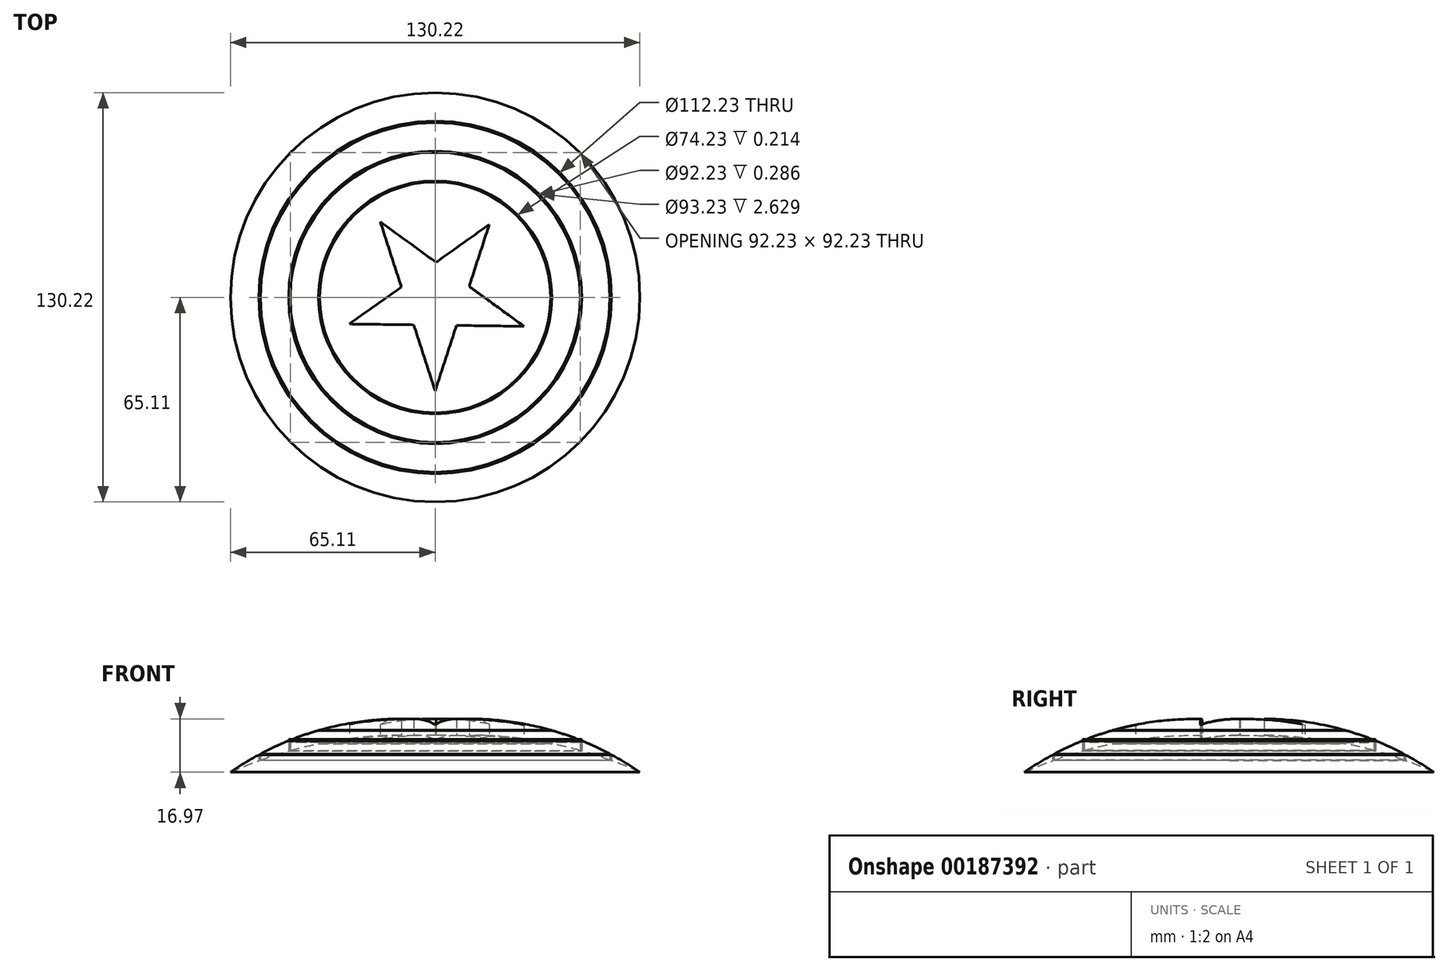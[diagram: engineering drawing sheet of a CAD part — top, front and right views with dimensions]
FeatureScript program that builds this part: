
annotation { "Feature Type Name" : "Feature", "Feature Type Description" : "" }
export const myFeature = defineFeature(function(context is Context, id is Id, definition is map)
    precondition{}
    {
        {
            var Q0;
            Q0=qCreatedBy(makeId("Front.planeOp"),FACE);
            var sketch = newSketch(context, id + "F0", { "sketchPlane" : qUnion([Q0])});
            skArc(sketch, "E0", {"start": v(65.11, 0) * mm, "mid": v(34.05, 14.12) * mm, "end": v(0, 16.34) * mm});
            skLineSegment(sketch, "E1", {"start": v(0, 16.34) * mm, "end": v(0, 11.34) * mm});
            skArc(sketch, "E2", {"start": v(65.11, 0) * mm, "mid": v(33.28, 9.81) * mm, "end": v(0, 11.34) * mm});
            skSolve(sketch);
        }
        {
            var Q0;
            Q0=makeQuery(id+"F0.imprint","IMPRINT",FACE,{"disambiguationData":[TD([[makeQuery(id+"F0.imprint","IMPRINT",EDGE,{"derivedFrom":sQuery(id+"F0.wireOp",EDGE,"E0")}),1.0]])]});
            var Q1;
            Q1=sQuery(id+"F0.wireOp",EDGE,"E1");
            revolve(context, id + "F1", {"entities" : qUnion([Q0]), "axis" : qUnion([Q1]), "revolveType" : RevolveType.FULL});
        }
        {
            var Q0;
            Q0=qCreatedBy(makeId("Top.planeOp"),FACE);
            var sketch = newSketch(context, id + "F2", { "sketchPlane" : qUnion([Q0])});
            skCircle(sketch, "E3", {"center": v(0, 0) * mm, "radius": 56.11 * mm});
            skCircle(sketch, "E4", {"center": v(0, 0) * mm, "radius": 55.61 * mm});
            skCircle(sketch, "E5", {"center": v(0, 0) * mm, "radius": 46.61 * mm});
            skCircle(sketch, "E6", {"center": v(0, 0) * mm, "radius": 46.11 * mm});
            skCircle(sketch, "E7", {"center": v(0, 0) * mm, "radius": 37.11 * mm});
            skCircle(sketch, "E8", {"center": v(0, 0) * mm, "radius": 36.61 * mm});
            skSolve(sketch);
        }
        {
            var Q0;
            Q0=makeQuery(id+"F2.imprint","IMPRINT",FACE,{"disambiguationData":[TD([[makeQuery(id+"F2.imprint","IMPRINT",EDGE,{"derivedFrom":sQuery(id+"F2.wireOp",EDGE,"E3")}),1.0]])]});
            var Q1;
            Q1=makeQuery(id+"F2.imprint","IMPRINT",FACE,{"disambiguationData":[TD([[makeQuery(id+"F2.imprint","IMPRINT",EDGE,{"derivedFrom":sQuery(id+"F2.wireOp",EDGE,"E5")}),1.0]])]});
            var Q2;
            Q2=makeQuery(id+"F2.imprint","IMPRINT",FACE,{"disambiguationData":[TD([[makeQuery(id+"F2.imprint","IMPRINT",EDGE,{"derivedFrom":sQuery(id+"F2.wireOp",EDGE,"E7")}),1.0]])]});
            extrude(context, id + "F3", {"entities" : qUnion([Q0, Q1, Q2]), "operationType" : NewBodyOperationType.REMOVE, "depth" : 9.5 * mm});
        }
        {
            var Q0;
            Q0=qCreatedBy(makeId("Top.planeOp"),FACE);
            var sketch = newSketch(context, id + "F4", { "sketchPlane" : qUnion([Q0])});
            skArc(sketch, "E9.cCircle", {"start": v(-1.88, -24) * mm, "mid": v(0, -24.07) * mm, "end": v(1.86, -24) * mm, "construction": true});
            skLineSegment(sketch, "E9.4", {"start": v(17.5, 24.06) * mm, "end": v(17.66, 23.53) * mm});
            skLineSegment(sketch, "E10", {"start": v(0, -29.75) * mm, "end": v(-6.83, -8.74) * mm});
            skLineSegment(sketch, "E11", {"start": v(0, -29.75) * mm, "end": v(6.77, -8.92) * mm});
            skLineSegment(sketch, "E12", {"start": v(17.66, 23.53) * mm, "end": v(0.28, 11.16) * mm});
            skLineSegment(sketch, "E13", {"start": v(-27.28, -8.47) * mm, "end": v(-6.83, -8.74) * mm});
            skLineSegment(sketch, "E14", {"start": v(28.29, -9.2) * mm, "end": v(10.8, 3.5) * mm});
            skLineSegment(sketch, "E15.trimOffspring", {"start": v(-10.74, 3.31) * mm, "end": v(-28.3, -9.18) * mm});
            skLineSegment(sketch, "E16.trimOffspring", {"start": v(-10.74, 3.31) * mm, "end": v(-17.48, 24.07) * mm});
            skLineSegment(sketch, "E17.trimOffspring", {"start": v(6.77, -8.92) * mm, "end": v(28.29, -9.2) * mm});
            skLineSegment(sketch, "E18.trimOffspring", {"start": v(10.8, 3.5) * mm, "end": v(17.5, 24.06) * mm});
            skLineSegment(sketch, "E19.trimOffspring", {"start": v(0.28, 11.16) * mm, "end": v(-17.48, 24.07) * mm});
            skArc(sketch, "E20.trimOffspring", {"start": v(22.27, -9.12) * mm, "mid": v(22.9, -7.4) * mm, "end": v(23.4, -5.64) * mm, "construction": true});
            skArc(sketch, "E21.trimOffspring", {"start": v(15.62, 18.3) * mm, "mid": v(14.36, 19.31) * mm, "end": v(13.03, 20.23) * mm, "construction": true});
            skArc(sketch, "E22.trimOffspring", {"start": v(-12.58, 20.51) * mm, "mid": v(-14.14, 19.47) * mm, "end": v(-15.6, 18.32) * mm, "construction": true});
            skArc(sketch, "E23.trimOffspring", {"start": v(-23.38, -5.69) * mm, "mid": v(-22.99, -7.12) * mm, "end": v(-22.5, -8.53) * mm, "construction": true});
            skSolve(sketch);
        }
        {
            var Q0;
            Q0=makeQuery(id+"F4.imprint","IMPRINT",FACE,{"disambiguationData":[TD([[makeQuery(id+"F4.imprint","IMPRINT",EDGE,{"derivedFrom":sQuery(id+"F4.wireOp",EDGE,"E10")}),-1.0]])]});
            extrude(context, id + "F5", {"entities" : qUnion([Q0]), "operationType" : NewBodyOperationType.REMOVE, "depth" : 25 * mm});
        }
        {
            var Q0;
            Q0=makeQuery(id+"F3.boolean.opBoolean","COPY",FACE,{"derivedFrom":makeQuery(id+"F3.opExtrude","CAP_FACE",FACE,{"disambiguationData":[OSD([sQuery(id+"F2.wireOp",EDGE,"E7"),sQuery(id+"F2.wireOp",EDGE,"E8")])],"isStart":false})});
            extrude(context, id + "F6", {"entities" : qUnion([Q0]), "operationType" : NewBodyOperationType.ADD, "oppositeDirection" : true, "depth" : 1 * mm, "hasSecondDirection" : true, "secondDirectionOppositeDirection" : false, "secondDirectionDepth" : .1 * mm});
        }
        {
            var Q0;
            Q0=makeQuery(id+"F3.boolean.opBoolean","COPY",FACE,{"derivedFrom":makeQuery(id+"F3.opExtrude","CAP_FACE",FACE,{"disambiguationData":[OSD([sQuery(id+"F2.wireOp",EDGE,"E5"),sQuery(id+"F2.wireOp",EDGE,"E6")])],"isStart":false})});
            extrude(context, id + "F7", {"entities" : qUnion([Q0]), "operationType" : NewBodyOperationType.ADD, "oppositeDirection" : true, "depth" : 1 * mm, "hasSecondDirection" : true, "secondDirectionOppositeDirection" : false, "secondDirectionDepth" : .1 * mm});
        }
        {
            var Q0;
            Q0=makeQuery(id+"F6.opExtrude","CAP_FACE",FACE,{"disambiguationData":[OSD([sQuery(id+"F2.wireOp",EDGE,"E7"),sQuery(id+"F2.wireOp",EDGE,"E8")])],"isStart":true});
            extrude(context, id + "F8", {"entities" : qUnion([Q0]), "operationType" : NewBodyOperationType.ADD, "oppositeDirection" : true, "depth" : 4 * mm, "hasSecondDirection" : true, "secondDirectionOppositeDirection" : false, "secondDirectionDepth" : .1 * mm});
        }
    });
